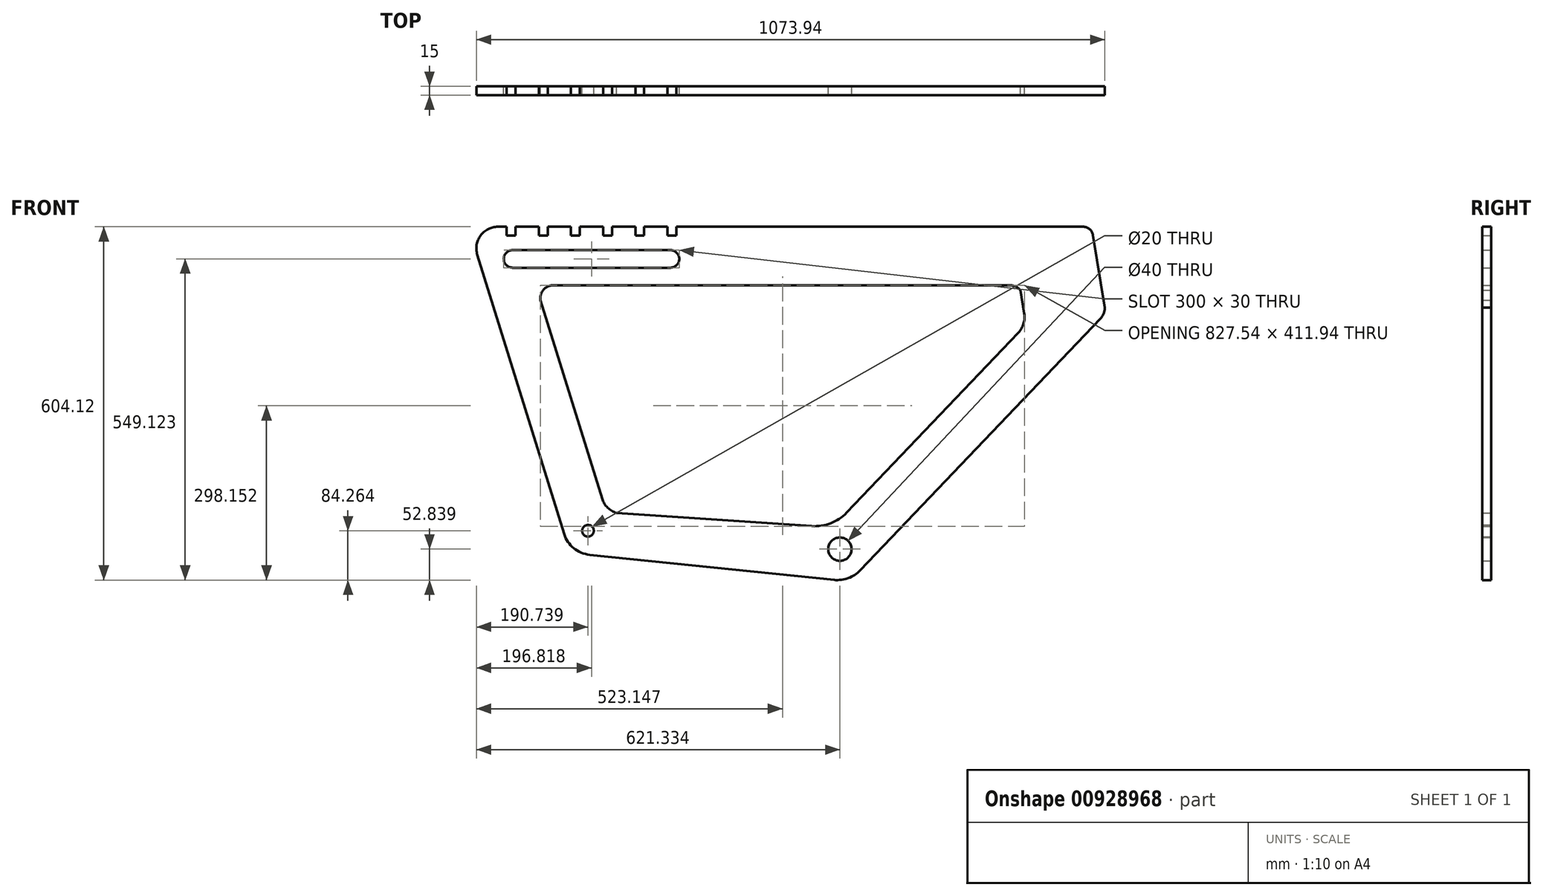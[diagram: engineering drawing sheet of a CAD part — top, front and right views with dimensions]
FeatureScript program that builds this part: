
annotation { "Feature Type Name" : "Feature", "Feature Type Description" : "" }
export const myFeature = defineFeature(function(context is Context, id is Id, definition is map)
    precondition{}
    {
        {
            assignVariable(context, id + "F0", {"name" : "Epbois", "anyValue" : 15});
        }
        {
            var Q0;
            Q0=qCreatedBy(makeId("Front.planeOp"),FACE);
            var sketch = newSketch(context, id + "F1", { "sketchPlane" : qUnion([Q0])});
            skLineSegment(sketch, "E0", {"start": v(-216.56, -92.36) * mm, "end": v(201.24, -135.33) * mm});
            skLineSegment(sketch, "E1", {"start": v(-408.5, 420.74) * mm, "end": v(-260.09, -56.73) * mm});
            skLineSegment(sketch, "E2", {"start": v(-373.33, 468.5) * mm, "end": v(626.67, 468.5) * mm});
            skLineSegment(sketch, "E3", {"start": v(246.31, -118.7) * mm, "end": v(656.36, 311.29) * mm});
            skArc(sketch, "E4", {"start": v(-373.33, 468.5) * mm, "mid": v(-402.98, 453.51) * mm, "end": v(-408.5, 420.74) * mm});
            skArc(sketch, "E5", {"start": v(-260.09, -56.73) * mm, "mid": v(-243.67, -81.08) * mm, "end": v(-216.56, -92.36) * mm});
            skLineSegment(sketch, "E6", {"start": v(-278.83, 368.5) * mm, "end": v(501.09, 368.5) * mm});
            skArc(sketch, "E7", {"start": v(643.77, 453.82) * mm, "mid": v(637.94, 464.33) * mm, "end": v(626.67, 468.5) * mm});
            skArc(sketch, "E8", {"start": v(656.36, 311.29) * mm, "mid": v(661.97, 320.13) * mm, "end": v(663.78, 330.44) * mm});
            skLineSegment(sketch, "E9", {"start": v(-300.48, 342.76) * mm, "end": v(-194.82, 2.82) * mm});
            skLineSegment(sketch, "E10", {"start": v(222.81, -20.19) * mm, "end": v(516.06, 287.34) * mm});
            skArc(sketch, "E11", {"start": v(-278.83, 368.5) * mm, "mid": v(-295.65, 360.67) * mm, "end": v(-300.48, 342.76) * mm});
            skArc(sketch, "E12", {"start": v(-194.82, 2.82) * mm, "mid": v(-185.78, -11.98) * mm, "end": v(-170.8, -20.72) * mm});
            skArc(sketch, "E13", {"start": v(501.09, 368.5) * mm, "mid": v(511.44, 366.24) * mm, "end": v(519.9, 359.85) * mm});
            skLineSegment(sketch, "E14", {"start": v(-170.8, -20.72) * mm, "end": v(162.91, -43.33) * mm});
            skArc(sketch, "E15", {"start": v(162.91, -43.33) * mm, "mid": v(195.43, -38.4) * mm, "end": v(222.81, -20.19) * mm});
            skLineSegment(sketch, "E16", {"start": v(519.9, 359.85) * mm, "end": v(526.3, 320.36) * mm});
            skLineSegment(sketch, "E17", {"start": v(643.77, 453.82) * mm, "end": v(663.78, 330.44) * mm});
            skArc(sketch, "E18", {"start": v(201.24, -135.33) * mm, "mid": v(225.7, -132.25) * mm, "end": v(246.31, -118.7) * mm});
            skLineSegment(sketch, "E19.bottom", {"start": v(-358.33, 468.5) * mm, "end": v(-343.33, 468.5) * mm});
            skLineSegment(sketch, "E19.top", {"start": v(-358.33, 453.5) * mm, "end": v(-343.33, 453.5) * mm});
            skLineSegment(sketch, "E19.left", {"start": v(-358.33, 468.5) * mm, "end": v(-358.33, 453.5) * mm});
            skLineSegment(sketch, "E19.right", {"start": v(-343.33, 468.5) * mm, "end": v(-343.33, 453.5) * mm});
            skLineSegment(sketch, "E20.bottom", {"start": v(-348.34, 428.5) * mm, "end": v(-78.34, 428.5) * mm});
            skLineSegment(sketch, "E20.top", {"start": v(-348.34, 398.5) * mm, "end": v(-78.34, 398.5) * mm});
            skArc(sketch, "E21", {"start": v(-78.34, 398.5) * mm, "mid": v(-63.34, 413.5) * mm, "end": v(-78.34, 428.5) * mm});
            skArc(sketch, "E22", {"start": v(-348.34, 428.5) * mm, "mid": v(-363.34, 413.5) * mm, "end": v(-348.34, 398.5) * mm});
            skLineSegment(sketch, "E23.bottom", {"start": v(-303.33, 468.5) * mm, "end": v(-288.33, 468.5) * mm});
            skLineSegment(sketch, "E23.top", {"start": v(-303.33, 453.5) * mm, "end": v(-288.33, 453.5) * mm});
            skLineSegment(sketch, "E23.left", {"start": v(-303.33, 468.5) * mm, "end": v(-303.33, 453.5) * mm});
            skLineSegment(sketch, "E23.right", {"start": v(-288.33, 468.5) * mm, "end": v(-288.33, 453.5) * mm});
            skLineSegment(sketch, "E24.bottom", {"start": v(-248.33, 468.5) * mm, "end": v(-233.33, 468.5) * mm});
            skLineSegment(sketch, "E24.top", {"start": v(-248.33, 453.5) * mm, "end": v(-233.33, 453.5) * mm});
            skLineSegment(sketch, "E24.left", {"start": v(-248.33, 468.5) * mm, "end": v(-248.33, 453.5) * mm});
            skLineSegment(sketch, "E24.right", {"start": v(-233.33, 468.5) * mm, "end": v(-233.33, 453.5) * mm});
            skLineSegment(sketch, "E25.bottom", {"start": v(-193.33, 468.5) * mm, "end": v(-178.33, 468.5) * mm});
            skLineSegment(sketch, "E25.top", {"start": v(-193.33, 453.5) * mm, "end": v(-178.33, 453.5) * mm});
            skLineSegment(sketch, "E25.left", {"start": v(-193.33, 468.5) * mm, "end": v(-193.33, 453.5) * mm});
            skLineSegment(sketch, "E25.right", {"start": v(-178.33, 468.5) * mm, "end": v(-178.33, 453.5) * mm});
            skLineSegment(sketch, "E26.bottom", {"start": v(-138.33, 468.5) * mm, "end": v(-123.33, 468.5) * mm});
            skLineSegment(sketch, "E26.top", {"start": v(-138.33, 453.5) * mm, "end": v(-123.33, 453.5) * mm});
            skLineSegment(sketch, "E26.left", {"start": v(-138.33, 468.5) * mm, "end": v(-138.33, 453.5) * mm});
            skLineSegment(sketch, "E26.right", {"start": v(-123.33, 468.5) * mm, "end": v(-123.33, 453.5) * mm});
            skLineSegment(sketch, "E27.bottom", {"start": v(-83.33, 468.5) * mm, "end": v(-68.33, 468.5) * mm});
            skLineSegment(sketch, "E27.top", {"start": v(-83.33, 453.5) * mm, "end": v(-68.33, 453.5) * mm});
            skLineSegment(sketch, "E27.left", {"start": v(-83.33, 468.5) * mm, "end": v(-83.33, 453.5) * mm});
            skLineSegment(sketch, "E27.right", {"start": v(-68.33, 468.5) * mm, "end": v(-68.33, 453.5) * mm});
            skArc(sketch, "E28", {"start": v(516.06, 287.34) * mm, "mid": v(525.06, 302.65) * mm, "end": v(526.3, 320.36) * mm});
            skCircle(sketch, "E29", {"center": v(-219.42, -51.36) * mm, "radius": 10 * mm});
            skCircle(sketch, "E30", {"center": v(211.17, -82.78) * mm, "radius": 20 * mm});
            skSolve(sketch);
        }
        {
            var Q0;
            Q0=makeQuery(id+"F1.imprint","IMPRINT",FACE,{"disambiguationData":[TD([[makeQuery(id+"F1.imprint","IMPRINT",EDGE,{"derivedFrom":sQuery(id+"F1.wireOp",EDGE,"E0")}),1.0]])]});
            extrude(context, id + "F2", {"entities" : qUnion([Q0]), "endBound" : BoundingType.SYMMETRIC, "depth" : (getVariable(context, 'Epbois')) * mm, "offsetDistance" : 25 * mm});
        }
    });
